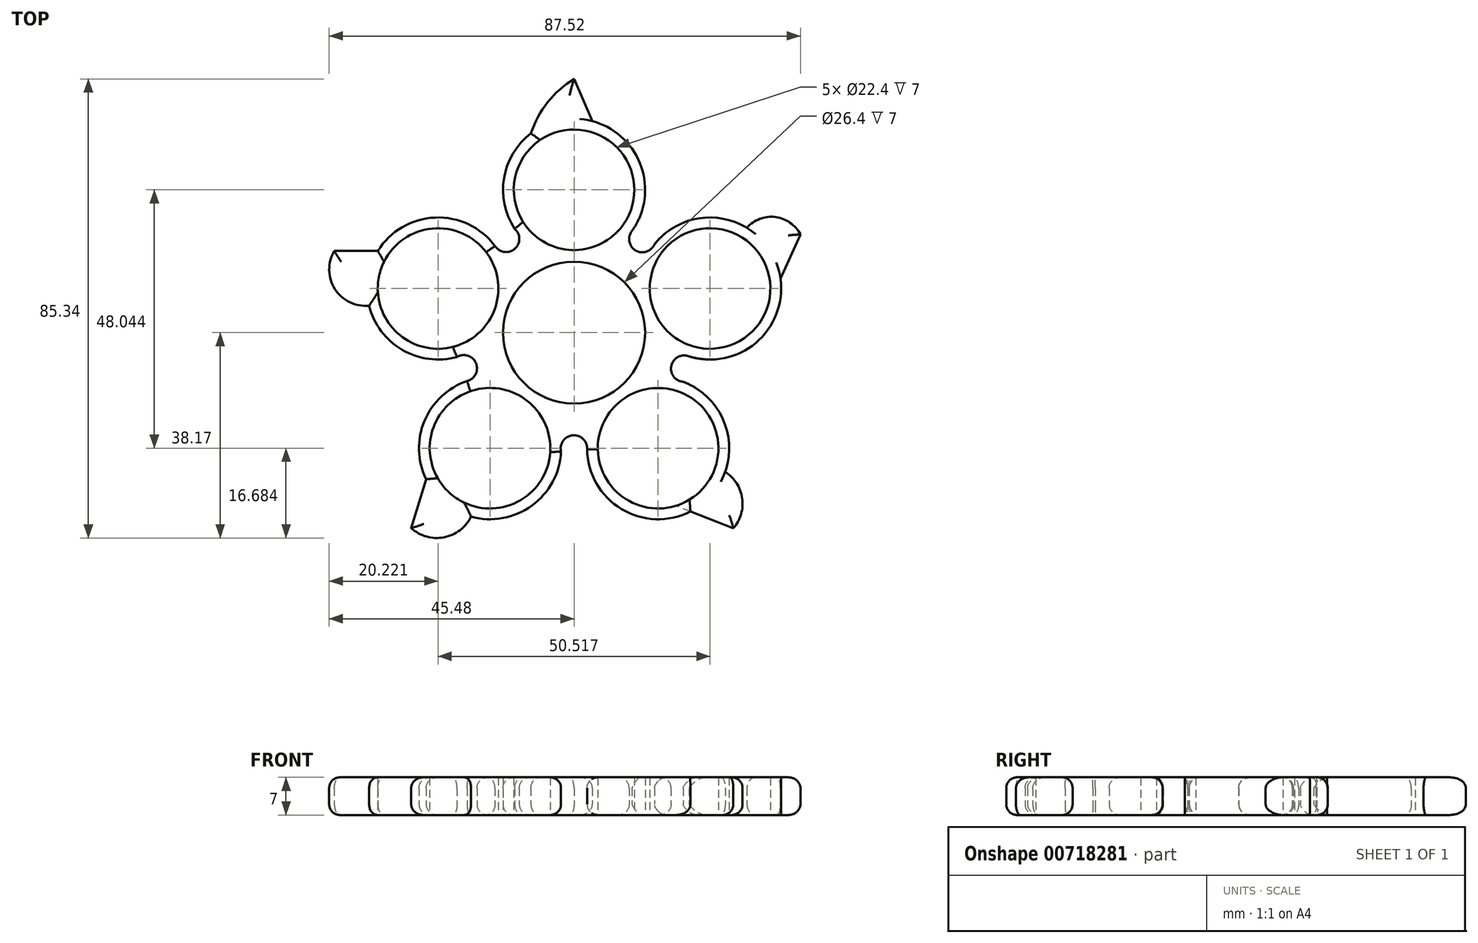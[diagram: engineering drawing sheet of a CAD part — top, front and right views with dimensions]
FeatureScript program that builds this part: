
annotation { "Feature Type Name" : "Feature", "Feature Type Description" : "" }
export const myFeature = defineFeature(function(context is Context, id is Id, definition is map)
    precondition{}
    {
        {
            var Q0;
            Q0=qCreatedBy(makeId("Top.planeOp"),FACE);
            var sketch = newSketch(context, id + "F0", { "sketchPlane" : qUnion([Q0])});
            skCircle(sketch, "E0", {"center": v(0, 0) * mm, "radius": 11.2 * mm});
            skCircle(sketch, "E1", {"center": v(0, 0) * mm, "radius": 13.2 * mm});
            skCircle(sketch, "E2", {"center": v(0, 26.56) * mm, "radius": 11.2 * mm});
            skArc(sketch, "E3", {"start": v(10.61, 18.7) * mm, "mid": v(-0.2, 39.76) * mm, "end": v(-10.36, 18.37) * mm});
            skArc(sketch, "E4.1.0", {"start": v(-14.51, 15.87) * mm, "mid": v(-37.88, 12.09) * mm, "end": v(-20.68, -4.17) * mm});
            skCircle(sketch, "E4.1.1", {"center": v(-25.26, 8.2) * mm, "radius": 11.2 * mm});
            skArc(sketch, "E4.2.0", {"start": v(-19.58, -8.9) * mm, "mid": v(-23.2, -32.29) * mm, "end": v(-2.42, -20.95) * mm});
            skCircle(sketch, "E4.2.1", {"center": v(-15.61, -21.49) * mm, "radius": 11.2 * mm});
            skArc(sketch, "E4.3.0", {"start": v(2.41, -21.37) * mm, "mid": v(23.54, -32.04) * mm, "end": v(19.18, -8.78) * mm});
            skCircle(sketch, "E4.3.1", {"center": v(15.61, -21.49) * mm, "radius": 11.2 * mm});
            skArc(sketch, "E4.4.0", {"start": v(21.07, -4.31) * mm, "mid": v(37.75, 12.48) * mm, "end": v(14.27, 15.53) * mm});
            skCircle(sketch, "E4.4.1", {"center": v(25.26, 8.2) * mm, "radius": 11.2 * mm});
            skArc(sketch, "E5", {"start": v(-14.69, 16.11) * mm, "mid": v(-11.02, 15.58) * mm, "end": v(-11.02, 19.3) * mm});
            skArc(sketch, "E6.1.0", {"start": v(-19.86, -8.99) * mm, "mid": v(-18.23, -5.66) * mm, "end": v(-21.75, -4.52) * mm});
            skArc(sketch, "E6.2.0", {"start": v(2.41, -21.67) * mm, "mid": v(-0.25, -19.08) * mm, "end": v(-2.42, -22.09) * mm});
            skArc(sketch, "E6.3.0", {"start": v(21.35, -4.4) * mm, "mid": v(18.07, -6.13) * mm, "end": v(20.26, -9.13) * mm});
            skArc(sketch, "E6.4.0", {"start": v(10.78, 18.95) * mm, "mid": v(11.42, 15.3) * mm, "end": v(14.94, 16.44) * mm});
            skArc(sketch, "E7", {"start": v(0, 47.17) * mm, "mid": v(-4.9, 42.82) * mm, "end": v(-8.02, 37.04) * mm});
            skLineSegment(sketch, "E8", {"start": v(0, 47.17) * mm, "end": v(3.4, 39.31) * mm});
            skArc(sketch, "E9", {"start": v(-44.53, 15.2) * mm, "mid": v(-44.43, 8.12) * mm, "end": v(-38.07, 5.01) * mm});
            skLineSegment(sketch, "E10", {"start": v(-44.53, 15.2) * mm, "end": v(-36.46, 15.2) * mm});
            skArc(sketch, "E11", {"start": v(-30.26, -36.34) * mm, "mid": v(-24.16, -38.05) * mm, "end": v(-19.13, -34.2) * mm});
            skLineSegment(sketch, "E12", {"start": v(-30.26, -36.34) * mm, "end": v(-27.49, -27.25) * mm});
            skArc(sketch, "E13", {"start": v(29.58, -36.37) * mm, "mid": v(31.22, -30.77) * mm, "end": v(28.06, -25.87) * mm});
            skLineSegment(sketch, "E14", {"start": v(29.58, -36.37) * mm, "end": v(21.6, -33.25) * mm});
            skArc(sketch, "E15", {"start": v(42.04, 18.25) * mm, "mid": v(37.4, 21.49) * mm, "end": v(32.1, 19.5) * mm});
            skLineSegment(sketch, "E16", {"start": v(42.04, 18.25) * mm, "end": v(38.34, 10) * mm});
            skSolve(sketch);
        }
        {
            var Q0;
            Q0=makeQuery(id+"F0.imprint","IMPRINT",FACE,{"disambiguationData":[TD([[makeQuery(id+"F0.imprint","IMPRINT",EDGE,{"derivedFrom":sQuery(id+"F0.wireOp",EDGE,"E1")}),-1.0]])]});
            var Q1;
            {var subQ0=sQuery(id+"F0.wireOp",EDGE,"E13");Q1=makeQuery(id+"F0.imprint","IMPRINT",FACE,{"disambiguationData":[TD([[makeQuery(id+"F0.imprint","IMPRINT",EDGE,{"derivedFrom":subQ0}),1.0]])]});}
            var Q2;
            {var subQ0=sQuery(id+"F0.wireOp",EDGE,"E11");Q2=makeQuery(id+"F0.imprint","IMPRINT",FACE,{"disambiguationData":[TD([[makeQuery(id+"F0.imprint","IMPRINT",EDGE,{"derivedFrom":subQ0}),1.0]])]});}
            var Q3;
            {var subQ0=sQuery(id+"F0.wireOp",EDGE,"E15");Q3=makeQuery(id+"F0.imprint","IMPRINT",FACE,{"disambiguationData":[TD([[makeQuery(id+"F0.imprint","IMPRINT",EDGE,{"derivedFrom":subQ0}),1.0]])]});}
            var Q4;
            {var subQ0=sQuery(id+"F0.wireOp",EDGE,"E7");Q4=makeQuery(id+"F0.imprint","IMPRINT",FACE,{"disambiguationData":[TD([[makeQuery(id+"F0.imprint","IMPRINT",EDGE,{"derivedFrom":subQ0}),1.0]])]});}
            var Q5;
            {var subQ0=sQuery(id+"F0.wireOp",EDGE,"E9");Q5=makeQuery(id+"F0.imprint","IMPRINT",FACE,{"disambiguationData":[TD([[makeQuery(id+"F0.imprint","IMPRINT",EDGE,{"derivedFrom":subQ0}),1.0]])]});}
            extrude(context, id + "F1", {"entities" : qUnion([Q0, Q1, Q2, Q3, Q4, Q5]), "depth" : 7 * mm, "offsetDistance" : 25 * mm});
        }
        {
            var Q0;
            {var subQ0=sQuery(id+"F0.wireOp",EDGE,"E3");Q0=makeQuery(id+"F1.opExtrude","CAP_EDGE",EDGE,{"disambiguationData":[OSD([subQ0]),TDD([makeQuery(id+"F0.imprint","IMPRINT",EDGE,{"disambiguationData":[TD([[makeQuery(id+"F0.imprint","INTERSECT",VERTEX,{"disambiguationData":[OD(1.0)],"derivedFrom":[subQ0,sQuery(id+"F0.wireOp",EDGE,"E6.4.0")]}),-1.0]])],"derivedFrom":subQ0})])],"isStart":false});}
            var Q1;
            {var subQ0=sQuery(id+"F0.wireOp",EDGE,"E3");Q1=makeQuery(id+"F1.opExtrude","CAP_EDGE",EDGE,{"disambiguationData":[OSD([subQ0]),TDD([makeQuery(id+"F0.imprint","IMPRINT",EDGE,{"disambiguationData":[TD([[makeQuery(id+"F0.imprint","INTERSECT",VERTEX,{"disambiguationData":[OD(1.0)],"derivedFrom":[subQ0,sQuery(id+"F0.wireOp",EDGE,"E5")]}),1.0]])],"derivedFrom":subQ0})])],"isStart":false});}
            var Q2;
            Q2=makeQuery(id+"F1.opExtrude","CAP_EDGE",EDGE,{"disambiguationData":[OSD([sQuery(id+"F0.wireOp",EDGE,"E5")])],"isStart":false});
            var Q3;
            Q3=makeQuery(id+"F1.opExtrude","CAP_EDGE",EDGE,{"disambiguationData":[OSD([sQuery(id+"F0.wireOp",EDGE,"E7")])],"isStart":false});
            var Q4;
            Q4=makeQuery(id+"F1.opExtrude","CAP_EDGE",EDGE,{"disambiguationData":[OSD([sQuery(id+"F0.wireOp",EDGE,"E8")])],"isStart":false});
            var Q5;
            Q5=makeQuery(id+"F1.opExtrude","CAP_EDGE",EDGE,{"disambiguationData":[OSD([sQuery(id+"F0.wireOp",EDGE,"E6.4.0")])],"isStart":false});
            var Q6;
            {var subQ0=sQuery(id+"F0.wireOp",EDGE,"E4.4.0");Q6=makeQuery(id+"F1.opExtrude","CAP_EDGE",EDGE,{"disambiguationData":[OSD([subQ0]),TDD([makeQuery(id+"F0.imprint","IMPRINT",EDGE,{"disambiguationData":[TD([[makeQuery(id+"F0.imprint","INTERSECT",VERTEX,{"disambiguationData":[OD(1.0)],"derivedFrom":[subQ0,sQuery(id+"F0.wireOp",EDGE,"E6.4.0")]}),1.0]])],"derivedFrom":subQ0})])],"isStart":false});}
            var Q7;
            Q7=makeQuery(id+"F1.opExtrude","CAP_EDGE",EDGE,{"disambiguationData":[OSD([sQuery(id+"F0.wireOp",EDGE,"E15")])],"isStart":false});
            var Q8;
            Q8=makeQuery(id+"F1.opExtrude","CAP_EDGE",EDGE,{"disambiguationData":[OSD([sQuery(id+"F0.wireOp",EDGE,"E16")])],"isStart":false});
            var Q9;
            {var subQ0=sQuery(id+"F0.wireOp",EDGE,"E4.4.0");Q9=makeQuery(id+"F1.opExtrude","CAP_EDGE",EDGE,{"disambiguationData":[OSD([subQ0]),TDD([makeQuery(id+"F0.imprint","IMPRINT",EDGE,{"disambiguationData":[TD([[makeQuery(id+"F0.imprint","INTERSECT",VERTEX,{"disambiguationData":[OD(1.0)],"derivedFrom":[subQ0,sQuery(id+"F0.wireOp",EDGE,"E6.3.0")]}),-1.0]])],"derivedFrom":subQ0})])],"isStart":false});}
            var Q10;
            Q10=makeQuery(id+"F1.opExtrude","CAP_EDGE",EDGE,{"disambiguationData":[OSD([sQuery(id+"F0.wireOp",EDGE,"E6.3.0")])],"isStart":false});
            var Q11;
            {var subQ0=sQuery(id+"F0.wireOp",EDGE,"E4.3.0");Q11=makeQuery(id+"F1.opExtrude","CAP_EDGE",EDGE,{"disambiguationData":[OSD([subQ0]),TDD([makeQuery(id+"F0.imprint","IMPRINT",EDGE,{"disambiguationData":[TD([[makeQuery(id+"F0.imprint","INTERSECT",VERTEX,{"disambiguationData":[OD(1.0)],"derivedFrom":[subQ0,sQuery(id+"F0.wireOp",EDGE,"E6.3.0")]}),1.0]])],"derivedFrom":subQ0})])],"isStart":false});}
            var Q12;
            Q12=makeQuery(id+"F1.opExtrude","CAP_EDGE",EDGE,{"disambiguationData":[OSD([sQuery(id+"F0.wireOp",EDGE,"E13")])],"isStart":false});
            var Q13;
            Q13=makeQuery(id+"F1.opExtrude","CAP_EDGE",EDGE,{"disambiguationData":[OSD([sQuery(id+"F0.wireOp",EDGE,"E14")])],"isStart":false});
            var Q14;
            {var subQ0=sQuery(id+"F0.wireOp",EDGE,"E4.3.0");Q14=makeQuery(id+"F1.opExtrude","CAP_EDGE",EDGE,{"disambiguationData":[OSD([subQ0]),TDD([makeQuery(id+"F0.imprint","IMPRINT",EDGE,{"disambiguationData":[TD([[makeQuery(id+"F0.imprint","INTERSECT",VERTEX,{"disambiguationData":[OD(1.0)],"derivedFrom":[subQ0,sQuery(id+"F0.wireOp",EDGE,"E6.2.0")]}),-1.0]])],"derivedFrom":subQ0})])],"isStart":false});}
            var Q15;
            Q15=makeQuery(id+"F1.opExtrude","CAP_EDGE",EDGE,{"disambiguationData":[OSD([sQuery(id+"F0.wireOp",EDGE,"E6.2.0")])],"isStart":false});
            var Q16;
            {var subQ0=sQuery(id+"F0.wireOp",EDGE,"E4.2.0");Q16=makeQuery(id+"F1.opExtrude","CAP_EDGE",EDGE,{"disambiguationData":[OSD([subQ0]),TDD([makeQuery(id+"F0.imprint","IMPRINT",EDGE,{"disambiguationData":[TD([[makeQuery(id+"F0.imprint","INTERSECT",VERTEX,{"disambiguationData":[OD(1.0)],"derivedFrom":[subQ0,sQuery(id+"F0.wireOp",EDGE,"E6.2.0")]}),1.0]])],"derivedFrom":subQ0})])],"isStart":false});}
            var Q17;
            Q17=makeQuery(id+"F1.opExtrude","CAP_EDGE",EDGE,{"disambiguationData":[OSD([sQuery(id+"F0.wireOp",EDGE,"E11")])],"isStart":false});
            var Q18;
            Q18=makeQuery(id+"F1.opExtrude","CAP_EDGE",EDGE,{"disambiguationData":[OSD([sQuery(id+"F0.wireOp",EDGE,"E12")])],"isStart":false});
            var Q19;
            {var subQ0=sQuery(id+"F0.wireOp",EDGE,"E4.2.0");Q19=makeQuery(id+"F1.opExtrude","CAP_EDGE",EDGE,{"disambiguationData":[OSD([subQ0]),TDD([makeQuery(id+"F0.imprint","IMPRINT",EDGE,{"disambiguationData":[TD([[makeQuery(id+"F0.imprint","INTERSECT",VERTEX,{"disambiguationData":[OD(1.0)],"derivedFrom":[subQ0,sQuery(id+"F0.wireOp",EDGE,"E6.1.0")]}),-1.0]])],"derivedFrom":subQ0})])],"isStart":false});}
            var Q20;
            Q20=makeQuery(id+"F1.opExtrude","CAP_EDGE",EDGE,{"disambiguationData":[OSD([sQuery(id+"F0.wireOp",EDGE,"E6.1.0")])],"isStart":false});
            var Q21;
            {var subQ0=sQuery(id+"F0.wireOp",EDGE,"E4.1.0");Q21=makeQuery(id+"F1.opExtrude","CAP_EDGE",EDGE,{"disambiguationData":[OSD([subQ0]),TDD([makeQuery(id+"F0.imprint","IMPRINT",EDGE,{"disambiguationData":[TD([[makeQuery(id+"F0.imprint","INTERSECT",VERTEX,{"disambiguationData":[OD(1.0)],"derivedFrom":[subQ0,sQuery(id+"F0.wireOp",EDGE,"E6.1.0")]}),1.0]])],"derivedFrom":subQ0})])],"isStart":false});}
            var Q22;
            Q22=makeQuery(id+"F1.opExtrude","CAP_EDGE",EDGE,{"disambiguationData":[OSD([sQuery(id+"F0.wireOp",EDGE,"E9")])],"isStart":false});
            var Q23;
            Q23=makeQuery(id+"F1.opExtrude","CAP_EDGE",EDGE,{"disambiguationData":[OSD([sQuery(id+"F0.wireOp",EDGE,"E10")])],"isStart":false});
            var Q24;
            {var subQ0=sQuery(id+"F0.wireOp",EDGE,"E4.1.0");Q24=makeQuery(id+"F1.opExtrude","CAP_EDGE",EDGE,{"disambiguationData":[OSD([subQ0]),TDD([makeQuery(id+"F0.imprint","IMPRINT",EDGE,{"disambiguationData":[TD([[makeQuery(id+"F0.imprint","INTERSECT",VERTEX,{"disambiguationData":[OD(1.0)],"derivedFrom":[subQ0,sQuery(id+"F0.wireOp",EDGE,"E5")]}),-1.0]])],"derivedFrom":subQ0})])],"isStart":false});}
            fillet(context, id + "F2", {"entities" : qUnion([Q0, Q1, Q2, Q3, Q4, Q5, Q6, Q7, Q8, Q9, Q10, Q11, Q12, Q13, Q14, Q15, Q16, Q17, Q18, Q19, Q20, Q21, Q22, Q23, Q24]), "radius" : 2 * mm, "tangentPropagation" : true, "allowEdgeOverflow" : false});
        }
        {
            var Q0;
            Q0=makeQuery(id+"F1.opExtrude","CAP_EDGE",EDGE,{"disambiguationData":[OSD([sQuery(id+"F0.wireOp",EDGE,"E8")])],"isStart":true});
            var Q1;
            {var subQ0=sQuery(id+"F0.wireOp",EDGE,"E3");Q1=makeQuery(id+"F1.opExtrude","CAP_EDGE",EDGE,{"disambiguationData":[OSD([subQ0]),TDD([makeQuery(id+"F0.imprint","IMPRINT",EDGE,{"disambiguationData":[TD([[makeQuery(id+"F0.imprint","INTERSECT",VERTEX,{"disambiguationData":[OD(1.0)],"derivedFrom":[subQ0,sQuery(id+"F0.wireOp",EDGE,"E5")]}),1.0]])],"derivedFrom":subQ0})])],"isStart":true});}
            var Q2;
            Q2=makeQuery(id+"F1.opExtrude","CAP_EDGE",EDGE,{"disambiguationData":[OSD([sQuery(id+"F0.wireOp",EDGE,"E7")])],"isStart":true});
            var Q3;
            {var subQ0=sQuery(id+"F0.wireOp",EDGE,"E3");Q3=makeQuery(id+"F1.opExtrude","CAP_EDGE",EDGE,{"disambiguationData":[OSD([subQ0]),TDD([makeQuery(id+"F0.imprint","IMPRINT",EDGE,{"disambiguationData":[TD([[makeQuery(id+"F0.imprint","INTERSECT",VERTEX,{"disambiguationData":[OD(1.0)],"derivedFrom":[subQ0,sQuery(id+"F0.wireOp",EDGE,"E6.4.0")]}),-1.0]])],"derivedFrom":subQ0})])],"isStart":true});}
            var Q4;
            Q4=makeQuery(id+"F1.opExtrude","CAP_EDGE",EDGE,{"disambiguationData":[OSD([sQuery(id+"F0.wireOp",EDGE,"E6.4.0")])],"isStart":true});
            var Q5;
            {var subQ0=sQuery(id+"F0.wireOp",EDGE,"E4.4.0");Q5=makeQuery(id+"F1.opExtrude","CAP_EDGE",EDGE,{"disambiguationData":[OSD([subQ0]),TDD([makeQuery(id+"F0.imprint","IMPRINT",EDGE,{"disambiguationData":[TD([[makeQuery(id+"F0.imprint","INTERSECT",VERTEX,{"disambiguationData":[OD(1.0)],"derivedFrom":[subQ0,sQuery(id+"F0.wireOp",EDGE,"E6.4.0")]}),1.0]])],"derivedFrom":subQ0})])],"isStart":true});}
            var Q6;
            Q6=makeQuery(id+"F1.opExtrude","CAP_EDGE",EDGE,{"disambiguationData":[OSD([sQuery(id+"F0.wireOp",EDGE,"E15")])],"isStart":true});
            var Q7;
            Q7=makeQuery(id+"F1.opExtrude","CAP_EDGE",EDGE,{"disambiguationData":[OSD([sQuery(id+"F0.wireOp",EDGE,"E16")])],"isStart":true});
            var Q8;
            {var subQ0=sQuery(id+"F0.wireOp",EDGE,"E4.4.0");Q8=makeQuery(id+"F1.opExtrude","CAP_EDGE",EDGE,{"disambiguationData":[OSD([subQ0]),TDD([makeQuery(id+"F0.imprint","IMPRINT",EDGE,{"disambiguationData":[TD([[makeQuery(id+"F0.imprint","INTERSECT",VERTEX,{"disambiguationData":[OD(1.0)],"derivedFrom":[subQ0,sQuery(id+"F0.wireOp",EDGE,"E6.3.0")]}),-1.0]])],"derivedFrom":subQ0})])],"isStart":true});}
            var Q9;
            Q9=makeQuery(id+"F1.opExtrude","CAP_EDGE",EDGE,{"disambiguationData":[OSD([sQuery(id+"F0.wireOp",EDGE,"E6.3.0")])],"isStart":true});
            var Q10;
            {var subQ0=sQuery(id+"F0.wireOp",EDGE,"E4.3.0");Q10=makeQuery(id+"F1.opExtrude","CAP_EDGE",EDGE,{"disambiguationData":[OSD([subQ0]),TDD([makeQuery(id+"F0.imprint","IMPRINT",EDGE,{"disambiguationData":[TD([[makeQuery(id+"F0.imprint","INTERSECT",VERTEX,{"disambiguationData":[OD(1.0)],"derivedFrom":[subQ0,sQuery(id+"F0.wireOp",EDGE,"E6.3.0")]}),1.0]])],"derivedFrom":subQ0})])],"isStart":true});}
            var Q11;
            Q11=makeQuery(id+"F1.opExtrude","CAP_EDGE",EDGE,{"disambiguationData":[OSD([sQuery(id+"F0.wireOp",EDGE,"E13")])],"isStart":true});
            var Q12;
            {var subQ0=sQuery(id+"F0.wireOp",EDGE,"E4.3.0");Q12=makeQuery(id+"F1.opExtrude","CAP_EDGE",EDGE,{"disambiguationData":[OSD([subQ0]),TDD([makeQuery(id+"F0.imprint","IMPRINT",EDGE,{"disambiguationData":[TD([[makeQuery(id+"F0.imprint","INTERSECT",VERTEX,{"disambiguationData":[OD(1.0)],"derivedFrom":[subQ0,sQuery(id+"F0.wireOp",EDGE,"E6.2.0")]}),-1.0]])],"derivedFrom":subQ0})])],"isStart":true});}
            var Q13;
            Q13=makeQuery(id+"F1.opExtrude","CAP_EDGE",EDGE,{"disambiguationData":[OSD([sQuery(id+"F0.wireOp",EDGE,"E6.2.0")])],"isStart":true});
            var Q14;
            {var subQ0=sQuery(id+"F0.wireOp",EDGE,"E4.2.0");Q14=makeQuery(id+"F1.opExtrude","CAP_EDGE",EDGE,{"disambiguationData":[OSD([subQ0]),TDD([makeQuery(id+"F0.imprint","IMPRINT",EDGE,{"disambiguationData":[TD([[makeQuery(id+"F0.imprint","INTERSECT",VERTEX,{"disambiguationData":[OD(1.0)],"derivedFrom":[subQ0,sQuery(id+"F0.wireOp",EDGE,"E6.2.0")]}),1.0]])],"derivedFrom":subQ0})])],"isStart":true});}
            var Q15;
            Q15=makeQuery(id+"F1.opExtrude","CAP_EDGE",EDGE,{"disambiguationData":[OSD([sQuery(id+"F0.wireOp",EDGE,"E12")])],"isStart":true});
            var Q16;
            Q16=makeQuery(id+"F1.opExtrude","CAP_EDGE",EDGE,{"disambiguationData":[OSD([sQuery(id+"F0.wireOp",EDGE,"E11")])],"isStart":true});
            var Q17;
            {var subQ0=sQuery(id+"F0.wireOp",EDGE,"E4.2.0");Q17=makeQuery(id+"F1.opExtrude","CAP_EDGE",EDGE,{"disambiguationData":[OSD([subQ0]),TDD([makeQuery(id+"F0.imprint","IMPRINT",EDGE,{"disambiguationData":[TD([[makeQuery(id+"F0.imprint","INTERSECT",VERTEX,{"disambiguationData":[OD(1.0)],"derivedFrom":[subQ0,sQuery(id+"F0.wireOp",EDGE,"E6.1.0")]}),-1.0]])],"derivedFrom":subQ0})])],"isStart":true});}
            var Q18;
            Q18=makeQuery(id+"F1.opExtrude","CAP_EDGE",EDGE,{"disambiguationData":[OSD([sQuery(id+"F0.wireOp",EDGE,"E6.1.0")])],"isStart":true});
            var Q19;
            {var subQ0=sQuery(id+"F0.wireOp",EDGE,"E4.1.0");Q19=makeQuery(id+"F1.opExtrude","CAP_EDGE",EDGE,{"disambiguationData":[OSD([subQ0]),TDD([makeQuery(id+"F0.imprint","IMPRINT",EDGE,{"disambiguationData":[TD([[makeQuery(id+"F0.imprint","INTERSECT",VERTEX,{"disambiguationData":[OD(1.0)],"derivedFrom":[subQ0,sQuery(id+"F0.wireOp",EDGE,"E6.1.0")]}),1.0]])],"derivedFrom":subQ0})])],"isStart":true});}
            var Q20;
            Q20=makeQuery(id+"F1.opExtrude","CAP_EDGE",EDGE,{"disambiguationData":[OSD([sQuery(id+"F0.wireOp",EDGE,"E9")])],"isStart":true});
            var Q21;
            Q21=makeQuery(id+"F1.opExtrude","CAP_EDGE",EDGE,{"disambiguationData":[OSD([sQuery(id+"F0.wireOp",EDGE,"E10")])],"isStart":true});
            var Q22;
            {var subQ0=sQuery(id+"F0.wireOp",EDGE,"E4.1.0");Q22=makeQuery(id+"F1.opExtrude","CAP_EDGE",EDGE,{"disambiguationData":[OSD([subQ0]),TDD([makeQuery(id+"F0.imprint","IMPRINT",EDGE,{"disambiguationData":[TD([[makeQuery(id+"F0.imprint","INTERSECT",VERTEX,{"disambiguationData":[OD(1.0)],"derivedFrom":[subQ0,sQuery(id+"F0.wireOp",EDGE,"E5")]}),-1.0]])],"derivedFrom":subQ0})])],"isStart":true});}
            var Q23;
            Q23=makeQuery(id+"F1.opExtrude","CAP_EDGE",EDGE,{"disambiguationData":[OSD([sQuery(id+"F0.wireOp",EDGE,"E5")])],"isStart":true});
            fillet(context, id + "F3", {"entities" : qUnion([Q0, Q1, Q2, Q3, Q4, Q5, Q6, Q7, Q8, Q9, Q10, Q11, Q12, Q13, Q14, Q15, Q16, Q17, Q18, Q19, Q20, Q21, Q22, Q23]), "radius" : 2 * mm, "tangentPropagation" : true, "allowEdgeOverflow" : false});
        }
    });
